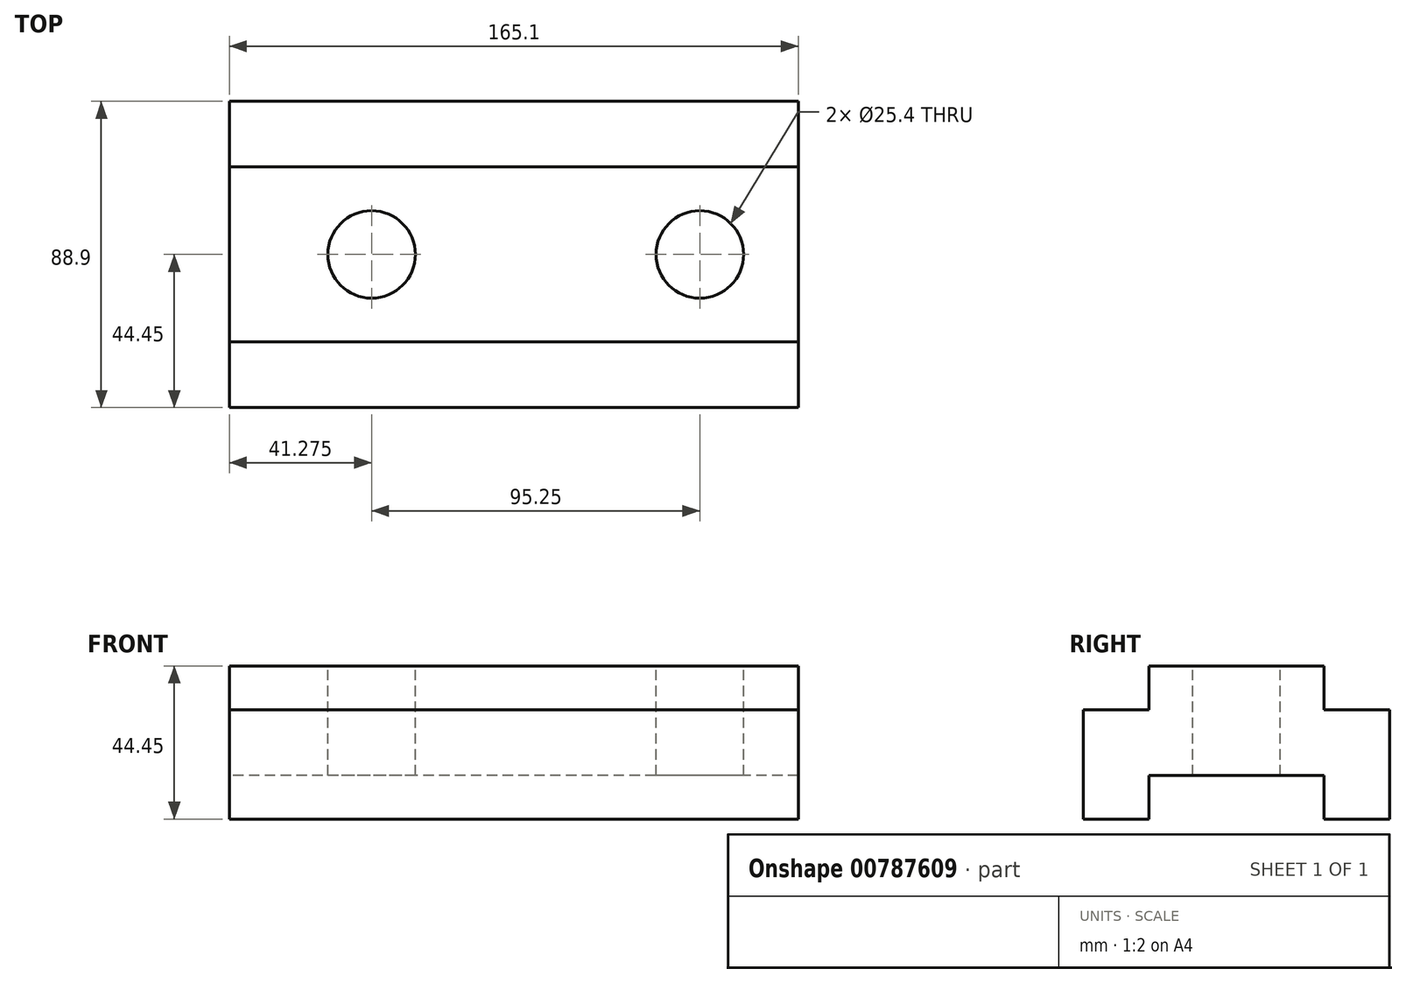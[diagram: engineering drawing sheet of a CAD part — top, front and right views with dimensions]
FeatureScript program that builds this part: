
annotation { "Feature Type Name" : "Feature", "Feature Type Description" : "" }
export const myFeature = defineFeature(function(context is Context, id is Id, definition is map)
    precondition{}
    {
        {
            var Q0;
            Q0=qCreatedBy(makeId("Right.planeOp"),FACE);
            var sketch = newSketch(context, id + "F0", { "sketchPlane" : qUnion([Q0])});
            skLineSegment(sketch, "E0", {"start": v(0, 0) * mm, "end": v(19.05, 0) * mm});
            skLineSegment(sketch, "E1", {"start": v(19.05, 0) * mm, "end": v(19.05, 12.7) * mm});
            skLineSegment(sketch, "E2", {"start": v(19.05, 12.7) * mm, "end": v(69.85, 12.7) * mm});
            skLineSegment(sketch, "E3", {"start": v(69.85, 12.7) * mm, "end": v(69.85, 0) * mm});
            skLineSegment(sketch, "E4", {"start": v(69.85, 0) * mm, "end": v(88.9, 0) * mm});
            skLineSegment(sketch, "E5", {"start": v(88.9, 0) * mm, "end": v(88.9, 31.75) * mm});
            skLineSegment(sketch, "E6", {"start": v(88.9, 31.75) * mm, "end": v(69.85, 31.75) * mm});
            skLineSegment(sketch, "E7", {"start": v(69.85, 31.75) * mm, "end": v(69.85, 44.45) * mm});
            skLineSegment(sketch, "E8", {"start": v(69.85, 44.45) * mm, "end": v(19.05, 44.45) * mm});
            skPoint(sketch, "E8.endSnap0", {"position": v(19.05, 6.35) * mm});
            skLineSegment(sketch, "E9", {"start": v(19.05, 44.45) * mm, "end": v(19.05, 31.75) * mm});
            skLineSegment(sketch, "E10", {"start": v(19.05, 31.75) * mm, "end": v(0, 31.75) * mm});
            skLineSegment(sketch, "E11", {"start": v(0, 31.75) * mm, "end": v(0, 0) * mm});
            skSolve(sketch);
        }
        {
            var Q0;
            Q0=makeQuery(id+"F0.imprint","IMPRINT",FACE,{"disambiguationData":[TD([[makeQuery(id+"F0.imprint","IMPRINT",EDGE,{"derivedFrom":sQuery(id+"F0.wireOp",EDGE,"E0")}),1.0]])]});
            extrude(context, id + "F1", {"entities" : qUnion([Q0]), "depth" : 165.1 * mm, "offsetDistance" : 25.4 * mm});
        }
        {
            var Q0;
            Q0=makeQuery(id+"F1.opExtrude","SWEPT_FACE",FACE,{"disambiguationData":[OSD([sQuery(id+"F0.wireOp",EDGE,"E8")])]});
            var sketch = newSketch(context, id + "F2", { "sketchPlane" : qUnion([Q0])});
            skLineSegment(sketch, "E12", {"start": v(0, 44.45) * mm, "end": v(41.28, 44.45) * mm, "construction": true});
            skLineSegment(sketch, "E13", {"start": v(41.28, 44.45) * mm, "end": v(136.53, 44.45) * mm, "construction": true});
            skCircle(sketch, "E14", {"center": v(41.28, 44.45) * mm, "radius": 12.7 * mm});
            skCircle(sketch, "E15", {"center": v(136.53, 44.45) * mm, "radius": 12.7 * mm});
            skSolve(sketch);
        }
        {
            var Q0;
            Q0=makeQuery(id+"F2.imprint","IMPRINT",FACE,{"disambiguationData":[TD([[makeQuery(id+"F2.imprint","IMPRINT",EDGE,{"derivedFrom":sQuery(id+"F2.wireOp",EDGE,"E14")}),1.0]])]});
            var Q1;
            Q1=makeQuery(id+"F2.imprint","IMPRINT",FACE,{"disambiguationData":[TD([[makeQuery(id+"F2.imprint","IMPRINT",EDGE,{"derivedFrom":sQuery(id+"F2.wireOp",EDGE,"E15")}),1.0]])]});
            extrude(context, id + "F3", {"entities" : qUnion([Q0, Q1]), "operationType" : NewBodyOperationType.REMOVE, "endBound" : BoundingType.THROUGH_ALL, "oppositeDirection" : true, "depth" : 25.4 * mm, "offsetDistance" : 25.4 * mm});
        }
    });
